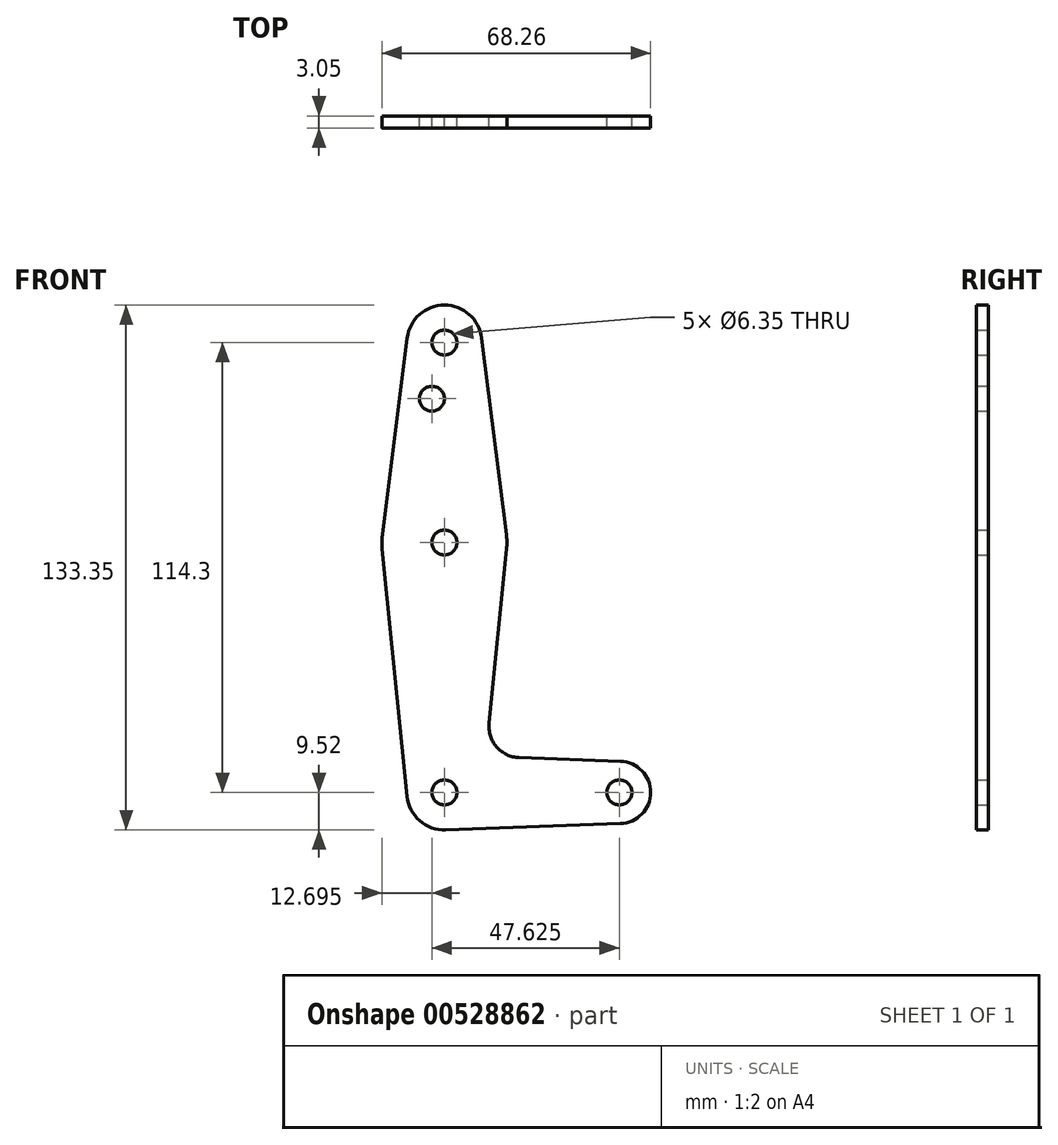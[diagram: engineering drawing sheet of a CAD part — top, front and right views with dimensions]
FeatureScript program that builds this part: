
annotation { "Feature Type Name" : "Feature", "Feature Type Description" : "" }
export const myFeature = defineFeature(function(context is Context, id is Id, definition is map)
    precondition{}
    {
        {
            var Q0;
            Q0=qCreatedBy(makeId("Front.planeOp"),FACE);
            var sketch = newSketch(context, id + "F0", { "sketchPlane" : qUnion([Q0])});
            skLineSegment(sketch, "E0", {"start": v(0, 0) * mm, "end": v(44.45, 0) * mm, "construction": true});
            skLineSegment(sketch, "E1", {"start": v(0, 0) * mm, "end": v(0, 114.3) * mm, "construction": true});
            skCircle(sketch, "E2", {"center": v(0, 63.5) * mm, "radius": 15.88 * mm});
            skCircle(sketch, "E3", {"center": v(0, 114.3) * mm, "radius": 9.53 * mm});
            skCircle(sketch, "E4", {"center": v(0, 0) * mm, "radius": 9.53 * mm});
            skCircle(sketch, "E5", {"center": v(44.45, 0) * mm, "radius": 7.94 * mm});
            skLineSegment(sketch, "E6", {"start": v(-9.45, 115.5) * mm, "end": v(-15.75, 65.48) * mm});
            skLineSegment(sketch, "E7", {"start": v(9.45, 115.5) * mm, "end": v(15.75, 65.48) * mm});
            skLineSegment(sketch, "E8", {"start": v(-15.8, 61.91) * mm, "end": v(-9.48, -0.95) * mm});
            skLineSegment(sketch, "E9", {"start": v(15.8, 61.91) * mm, "end": v(11.34, 17.6) * mm});
            skLineSegment(sketch, "E10", {"start": v(18.97, 8.85) * mm, "end": v(44.73, 7.93) * mm});
            skLineSegment(sketch, "E11", {"start": v(0.34, -9.52) * mm, "end": v(44.73, -7.93) * mm});
            skArc(sketch, "E12.filletArc", {"start": v(11.34, 17.6) * mm, "mid": v(13.26, 11.57) * mm, "end": v(18.97, 8.85) * mm});
            skCircle(sketch, "E13", {"center": v(0, 114.3) * mm, "radius": 3.18 * mm});
            skCircle(sketch, "E14", {"center": v(0, 63.5) * mm, "radius": 3.18 * mm});
            skCircle(sketch, "E15", {"center": v(0, 0) * mm, "radius": 3.18 * mm});
            skCircle(sketch, "E16", {"center": v(44.45, 0) * mm, "radius": 3.18 * mm});
            skCircle(sketch, "E17", {"center": v(-3.18, 100.03) * mm, "radius": 3.18 * mm});
            skSolve(sketch);
        }
        {
            var Q0;
            Q0 = qSketchRegion(id + "F0", true);
            extrude(context, id + "F1", {"entities" : qUnion([Q0]), "depth" : 3.05 * mm, "offsetDistance" : 25.4 * mm});
        }
    });
